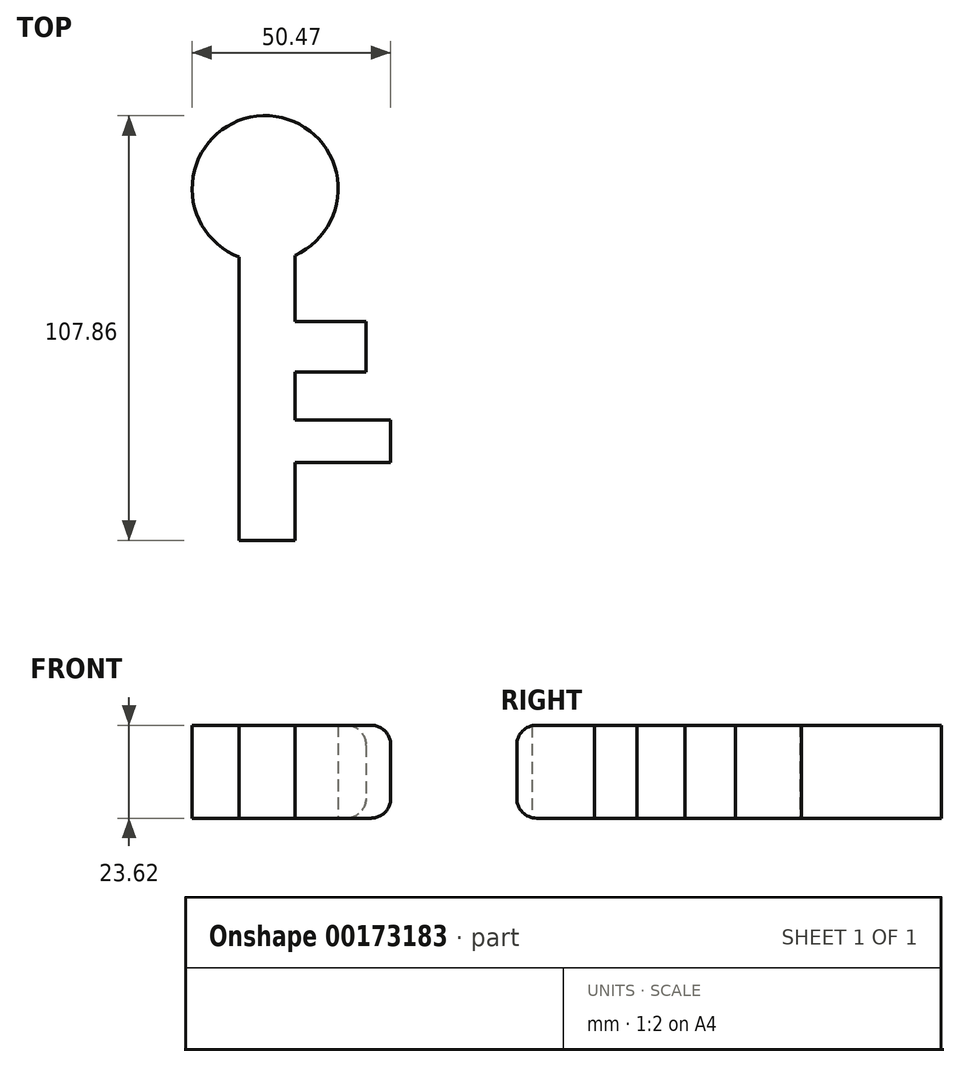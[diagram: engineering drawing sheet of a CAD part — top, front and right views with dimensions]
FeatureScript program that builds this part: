
annotation { "Feature Type Name" : "Feature", "Feature Type Description" : "" }
export const myFeature = defineFeature(function(context is Context, id is Id, definition is map)
    precondition{}
    {
        {
            var Q0;
            Q0=qCreatedBy(makeId("Top.planeOp"),FACE);
            var sketch = newSketch(context, id + "F0", { "sketchPlane" : qUnion([Q0])});
            skArc(sketch, "E0", {"start": v(16, 22.73) * mm, "mid": v(7.89, 58.2) * mm, "end": v(1.84, 22.32) * mm});
            skLineSegment(sketch, "E1", {"start": v(1.84, 22.32) * mm, "end": v(1.84, -48.48) * mm});
            skLineSegment(sketch, "E2", {"start": v(16, 22.73) * mm, "end": v(16, 14) * mm});
            skLineSegment(sketch, "E3", {"start": v(16, -49.65) * mm, "end": v(1.76, -49.65) * mm});
            skLineSegment(sketch, "E4", {"start": v(1.76, -49.65) * mm, "end": v(1.84, -45.73) * mm});
            skLineSegment(sketch, "E5", {"start": v(16, 5.97) * mm, "end": v(34.08, 5.97) * mm});
            skLineSegment(sketch, "E6", {"start": v(34.08, 5.97) * mm, "end": v(34.08, -6.95) * mm});
            skLineSegment(sketch, "E7", {"start": v(34.08, -6.95) * mm, "end": v(16, -6.95) * mm});
            skLineSegment(sketch, "E8", {"start": v(16, -19.1) * mm, "end": v(40.35, -19.1) * mm});
            skLineSegment(sketch, "E9", {"start": v(40.35, -19.1) * mm, "end": v(40.35, -29.87) * mm});
            skLineSegment(sketch, "E10", {"start": v(40.35, -29.87) * mm, "end": v(16, -29.87) * mm});
            skLineSegment(sketch, "E11.trimOffspring", {"start": v(16, 5.97) * mm, "end": v(16, 14) * mm});
            skLineSegment(sketch, "E12.trimOffspring", {"start": v(16, -29.87) * mm, "end": v(16, -49.65) * mm});
            skPoint(sketch, "E13.left.end.orphan", {"position": v(16, -25.76) * mm});
            skLineSegment(sketch, "E14", {"start": v(16, -19.1) * mm, "end": v(16, -6.95) * mm});
            skSolve(sketch);
        }
        {
            var Q0;
            {var subQ0=sQuery(id+"F0.wireOp",EDGE,"E0");Q0=makeQuery(id+"F0.imprint","IMPRINT",FACE,{"disambiguationData":[TD([[makeQuery(id+"F0.imprint","IMPRINT",EDGE,{"derivedFrom":subQ0}),1.0]])]});}
            extrude(context, id + "F1", {"entities" : qUnion([Q0]), "depth" : 23.62 * mm});
        }
        {
            var Q0;
            Q0=makeQuery(id+"F1.opExtrude","CAP_EDGE",EDGE,{"disambiguationData":[OSD([sQuery(id+"F0.wireOp",EDGE,"E9")])],"isStart":false});
            var Q1;
            Q1=makeQuery(id+"F1.opExtrude","CAP_EDGE",EDGE,{"disambiguationData":[OSD([sQuery(id+"F0.wireOp",EDGE,"E6")])],"isStart":false});
            var Q2;
            Q2=makeQuery(id+"F1.opExtrude","CAP_EDGE",EDGE,{"disambiguationData":[OSD([sQuery(id+"F0.wireOp",EDGE,"E3")])],"isStart":false});
            var Q3;
            Q3=makeQuery(id+"F1.opExtrude","CAP_EDGE",EDGE,{"disambiguationData":[OSD([sQuery(id+"F0.wireOp",EDGE,"E6")])],"isStart":true});
            var Q4;
            Q4=makeQuery(id+"F1.opExtrude","CAP_EDGE",EDGE,{"disambiguationData":[OSD([sQuery(id+"F0.wireOp",EDGE,"E9")])],"isStart":true});
            var Q5;
            Q5=makeQuery(id+"F1.opExtrude","CAP_EDGE",EDGE,{"disambiguationData":[OSD([sQuery(id+"F0.wireOp",EDGE,"E3")])],"isStart":true});
            fillet(context, id + "F2", {"entities" : qUnion([Q0, Q1, Q2, Q3, Q4, Q5]), "radius" : 5.08 * mm, "tangentPropagation" : true, "allowEdgeOverflow" : false});
        }
    });
